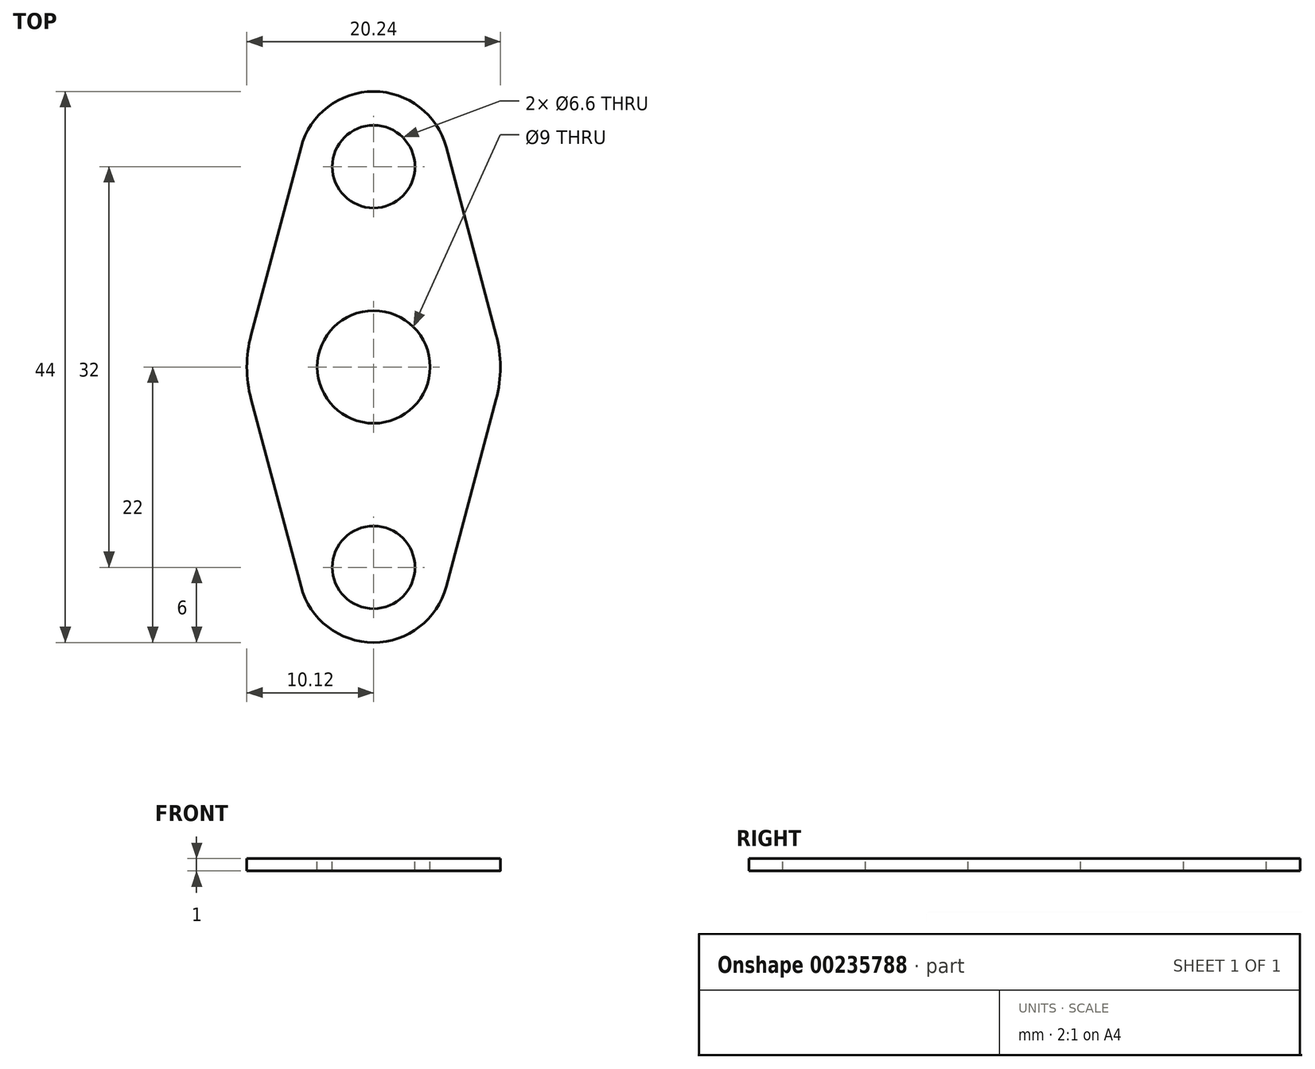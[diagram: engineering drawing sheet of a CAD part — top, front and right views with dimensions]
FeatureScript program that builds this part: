
annotation { "Feature Type Name" : "Feature", "Feature Type Description" : "" }
export const myFeature = defineFeature(function(context is Context, id is Id, definition is map)
    precondition{}
    {
        {
            var Q0;
            Q0=qCreatedBy(makeId("Top.planeOp"),FACE);
            var sketch = newSketch(context, id + "F0", { "sketchPlane" : qUnion([Q0])});
            skArc(sketch, "E0", {"start": v(5.8, 17.54) * mm, "mid": v(0, 22) * mm, "end": v(-5.8, 17.54) * mm});
            skArc(sketch, "E1.MirrorC", {"start": v(5.8, -17.54) * mm, "mid": v(0, -22) * mm, "end": v(-5.8, -17.54) * mm});
            skLineSegment(sketch, "E2", {"start": v(-5.8, 17.54) * mm, "end": v(-10.47, 0) * mm});
            skLineSegment(sketch, "E3", {"start": v(-10.47, 0) * mm, "end": v(-5.8, -17.54) * mm});
            skLineSegment(sketch, "E4.MirrorCS", {"start": v(5.8, 17.54) * mm, "end": v(10.47, 0) * mm});
            skLineSegment(sketch, "E5.MirrorCS", {"start": v(10.47, 0) * mm, "end": v(5.8, -17.54) * mm});
            skSolve(sketch);
        }
        {
            var Q0;
            Q0=makeQuery(id+"F0.imprint","IMPRINT",FACE,{"disambiguationData":[TD([[makeQuery(id+"F0.imprint","IMPRINT",EDGE,{"derivedFrom":sQuery(id+"F0.wireOp",EDGE,"E0")}),1.0]])]});
            extrude(context, id + "F1", {"entities" : qUnion([Q0]), "depth" : 1 * mm});
        }
        {
            var Q0;
            Q0=makeQuery(id+"F1.opExtrude","SWEPT_EDGE",EDGE,{"disambiguationData":[OSD([sQuery(id+"F0.wireOp",EDGE,"E4.MirrorCS"),sQuery(id+"F0.wireOp",EDGE,"E5.MirrorCS")])]});
            var Q1;
            Q1=makeQuery(id+"F1.opExtrude","SWEPT_EDGE",EDGE,{"disambiguationData":[OSD([sQuery(id+"F0.wireOp",EDGE,"E2"),sQuery(id+"F0.wireOp",EDGE,"E3")])]});
            fillet(context, id + "F2", {"entities" : qUnion([Q0, Q1]), "radius" : 10 * mm, "tangentPropagation" : true, "allowEdgeOverflow" : false});
        }
        {
            var Q0;
            Q0=makeQuery(id+"F1.opExtrude","CAP_FACE",FACE,{"disambiguationData":[OSD([sQuery(id+"F0.wireOp",EDGE,"E0"),sQuery(id+"F0.wireOp",EDGE,"E1.MirrorC"),sQuery(id+"F0.wireOp",EDGE,"E2"),sQuery(id+"F0.wireOp",EDGE,"E3"),sQuery(id+"F0.wireOp",EDGE,"E4.MirrorCS"),sQuery(id+"F0.wireOp",EDGE,"E5.MirrorCS")])],"isStart":false});
            var sketch = newSketch(context, id + "F3", { "sketchPlane" : qUnion([Q0])});
            skCircle(sketch, "E6", {"center": v(0, 0) * mm, "radius": 4.5 * mm});
            skCircle(sketch, "E7", {"center": v(0, 16) * mm, "radius": 3.3 * mm});
            skCircle(sketch, "E8.MirrorC", {"center": v(0, -16) * mm, "radius": 3.3 * mm});
            skSolve(sketch);
        }
        {
            var Q0;
            Q0=sQuery(id+"F3.wireOp",VERTEX,"E6.center");
            var Q1;
            Q1=makeQuery(id+"F1.opExtrude","SWEPT_BODY",BODY,{"disambiguationData":[OSD([sQuery(id+"F0.wireOp",EDGE,"E0"),sQuery(id+"F0.wireOp",EDGE,"E1.MirrorC"),sQuery(id+"F0.wireOp",EDGE,"E2"),sQuery(id+"F0.wireOp",EDGE,"E3"),sQuery(id+"F0.wireOp",EDGE,"E4.MirrorCS"),sQuery(id+"F0.wireOp",EDGE,"E5.MirrorCS")])]});
            hole(context, id + "F4", {"style" : HoleStyle.SIMPLE, "endStyle" : HoleEndStyle.THROUGH, "holeDiameter" : 9 * mm, "locations" : qUnion([Q0]), "scope" : qUnion([Q1]), "isTappedThrough" : true});
        }
        {
            var Q0;
            Q0=sQuery(id+"F3.wireOp",VERTEX,"E7.center");
            var Q1;
            Q1=sQuery(id+"F3.wireOp",VERTEX,"E8.MirrorC.center");
            var Q2;
            Q2=makeQuery(id+"F1.opExtrude","SWEPT_BODY",BODY,{"disambiguationData":[OSD([sQuery(id+"F0.wireOp",EDGE,"E0"),sQuery(id+"F0.wireOp",EDGE,"E1.MirrorC"),sQuery(id+"F0.wireOp",EDGE,"E2"),sQuery(id+"F0.wireOp",EDGE,"E3"),sQuery(id+"F0.wireOp",EDGE,"E4.MirrorCS"),sQuery(id+"F0.wireOp",EDGE,"E5.MirrorCS")])]});
            hole(context, id + "F5", {"style" : HoleStyle.SIMPLE, "endStyle" : HoleEndStyle.THROUGH, "holeDiameter" : 6.6 * mm, "locations" : qUnion([Q0, Q1]), "scope" : qUnion([Q2]), "isTappedThrough" : true});
        }
    });
